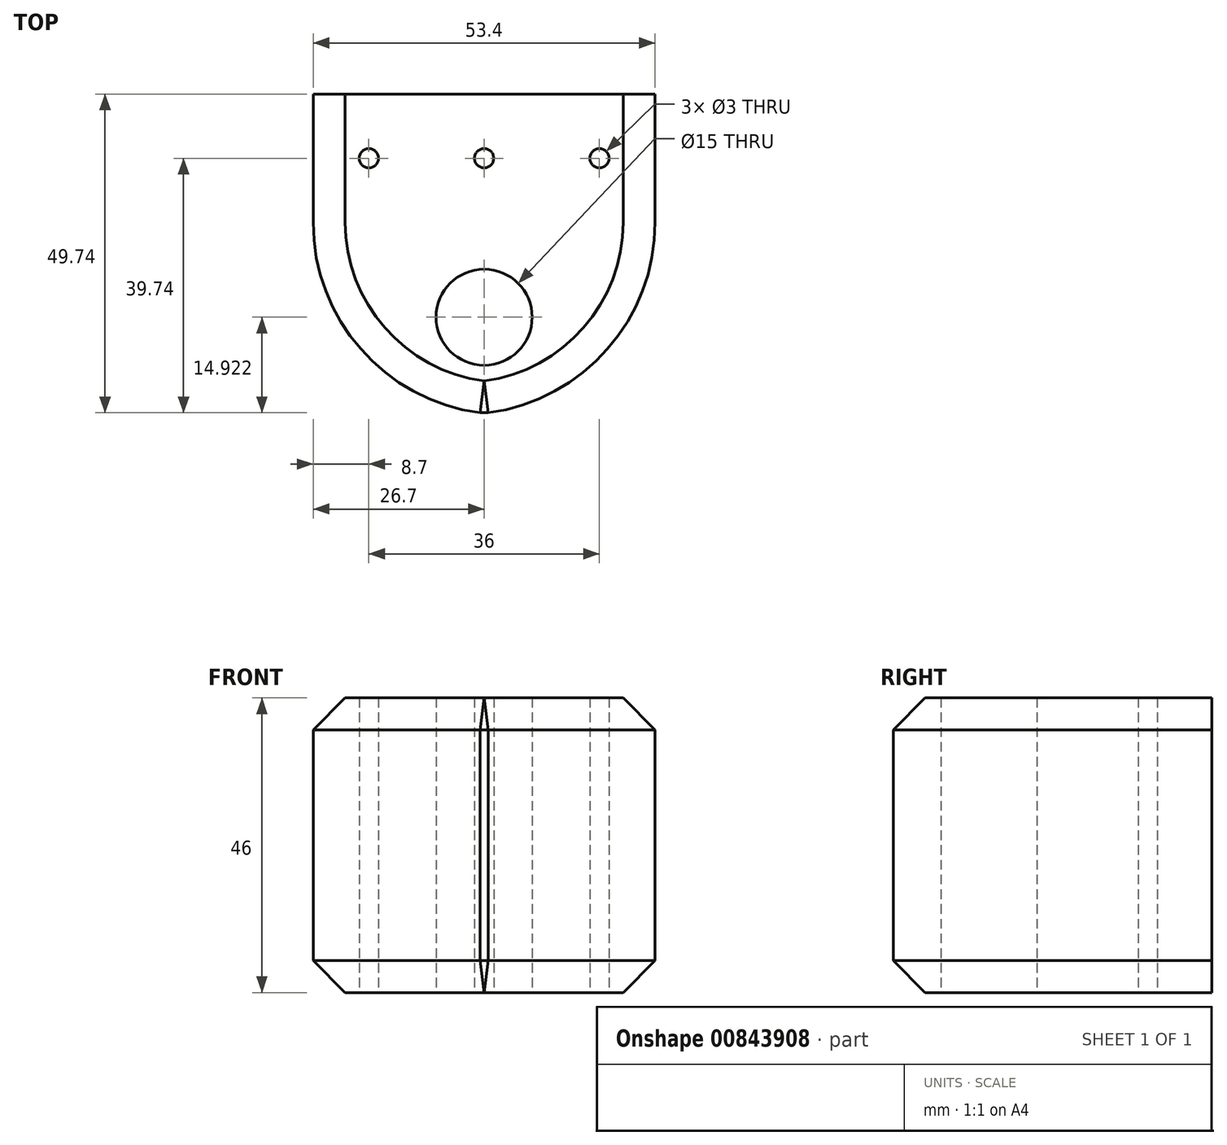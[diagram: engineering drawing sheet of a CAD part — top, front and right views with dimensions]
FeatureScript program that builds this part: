
annotation { "Feature Type Name" : "Feature", "Feature Type Description" : "" }
export const myFeature = defineFeature(function(context is Context, id is Id, definition is map)
    precondition{}
    {
        {
            var Q0;
            Q0=qCreatedBy(makeId("Top.planeOp"),FACE);
            var sketch = newSketch(context, id + "F0", { "sketchPlane" : qUnion([Q0])});
            skLineSegment(sketch, "E0.bottom", {"start": v(26.7, -10) * mm, "end": v(-26.7, -10) * mm});
            skLineSegment(sketch, "E0.top", {"start": v(26.7, 10) * mm, "end": v(-26.7, 10) * mm});
            skLineSegment(sketch, "E0.left", {"start": v(26.7, -10) * mm, "end": v(26.7, 10) * mm});
            skLineSegment(sketch, "E0.right", {"start": v(-26.7, -10) * mm, "end": v(-26.7, 10) * mm});
            skPoint(sketch, "E0.middle", {"position": v(0, 0) * mm});
            skCircle(sketch, "E1", {"center": v(0, 0) * mm, "radius": 1.5 * mm});
            skCircle(sketch, "E2", {"center": v(18, 0) * mm, "radius": 1.5 * mm});
            skCircle(sketch, "E3", {"center": v(-18, 0) * mm, "radius": 1.5 * mm});
            skLineSegment(sketch, "E4.bottom", {"start": v(-26.7, -10) * mm, "end": v(26.7, -10) * mm});
            skLineSegment(sketch, "E4.left", {"start": v(-26.7, -10) * mm, "end": v(-26.7, -10) * mm});
            skLineSegment(sketch, "E4.right", {"start": v(26.7, -10) * mm, "end": v(26.7, -10) * mm});
            skPoint(sketch, "E5.visualSharp", {"position": v(-26.7, -40) * mm});
            skArc(sketch, "E5.filletArc", {"start": v(-26.7, -10) * mm, "mid": v(-19.05, -30.01) * mm, "end": v(0, -39.82) * mm});
            skPoint(sketch, "E6.visualSharp", {"position": v(26.7, -40) * mm});
            skArc(sketch, "E6.filletArc", {"start": v(0, -39.82) * mm, "mid": v(19.05, -30.01) * mm, "end": v(26.7, -10) * mm});
            skCircle(sketch, "E7", {"center": v(0, -24.82) * mm, "radius": 7.5 * mm});
            skSolve(sketch);
        }
        {
            var Q0;
            Q0 = qSketchRegion(id + "F0", true);
            extrude(context, id + "F1", {"entities" : qUnion([Q0]), "depth" : 46 * mm, "offsetDistance" : 25 * mm});
        }
        {
            var Q0;
            Q0=makeQuery(id+"F1.opExtrude","CAP_EDGE",EDGE,{"disambiguationData":[OSD([sQuery(id+"F0.wireOp",EDGE,"E5.filletArc")])],"isStart":true});
            var Q1;
            Q1=makeQuery(id+"F1.opExtrude","SWEPT_FACE",FACE,{"disambiguationData":[OSD([sQuery(id+"F0.wireOp",EDGE,"E5.filletArc")])]});
            var Q2;
            Q2=makeQuery(id+"F1.opExtrude","SWEPT_FACE",FACE,{"disambiguationData":[OSD([sQuery(id+"F0.wireOp",EDGE,"E6.filletArc")])]});
            chamfer(context, id + "F2", {"entities" : qUnion([Q0, Q1, Q2]), "width" : 5 * mm, "tangentPropagation" : true});
        }
    });
